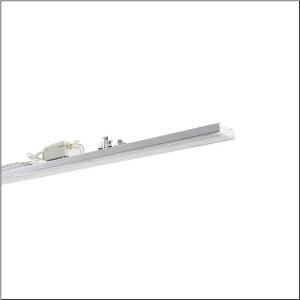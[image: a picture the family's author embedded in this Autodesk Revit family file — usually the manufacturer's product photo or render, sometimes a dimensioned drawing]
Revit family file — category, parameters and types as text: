
# Revit family: licross_21_recessed_mo_52tl1edn465g
name_source: partatom
category: Lighting Fixtures
units: mm (PartAtom-declared; Revit-internal decimal feet)

## family parameters
Cut with Voids When Loaded = No
Host = Face
Light Source = No
Part Type = Normal
Room Calculation Point = No
Round Connector Dimension = Use Diameter
Shared = No

## types (1)
- --- (1 x LED, 6990 lm, 39.3 W, 4000K)
    Apparent Load = 39 VA
    CIE Flux Codes = 85 95 99 100 100
    Color Rendering = 80
    Color Temperature = 4000K
    Default Elevation = 1800 mm
    Description = Licross 21 Recessed MO, luminaire insert, of sheet steel, galvanised, coil coated, white, length: 1.500mm, width: 66mm, height: 67mm, LED rated luminous flux: 6.990lm, light colour: 840, SDCM (Standard Deviation of Colour Matching)MacAdam ≤ 3 SDCM (initial), control gear: DALI 2, with plug, 5-pole, with phase selection, mains connection: 220..240V, AC, 50/60Hz, rated input power: 39W, internal wiring halogen-free, primary light control with lens, of plastic, primary optical cover: cover, of PMMA, light emission: direct distribution, primary light characteristic: symmetric, protection rating (complete): IP40, insulation class (complete): insulation class I (protective earthing), certification: CE, ENEC, VDE, UKCA, protection symbol: D if used in an environment without relevant dust loads with corresponding accessories, impact resistance: IK06, permissible ambient temperature for indoor applications: -25..+40°C, corresponds to IFS (International Featured Standards) requirements for safety and quality in the food industry, reducing of maximum allowable ambient temperature of 5°C with ceiling mounting, LABS conformity tested according to VDMA 24364:2018-05, The light source and the operating device comply with the requirements of the Ecodesign Regulation (EU) 2019/2020 and are replaceable in accordance with this regulation, packaging unit: 1 piece
    Height = 58 mm
    Lamp = 1 x LED
    Lamp Light Flux = 6990 lm
    Lamp Power = 39.3 W
    Lamp count = 1
    Length = 1500 mm
    Luminous efficacy = 178 lm/W
    Manufacturer = Siteco
    ModVariant = No
    Model = 52TL1EDN465G
    Mounting Place = Ceiling
    Mounting Type = Pendant
    Number of Poles = 1
    OnlyDefault = Yes
    Power Factor = 1
    Product Name = Licross 21 Recessed MO
    Product group = luminaire insert | ceiling pendant
    ProductGroupID = 901
    Protection Class = Protection class I
    Protection Degree = IP 40
    RLX_Detail_Level = 1
    RLX_Emergency_Light_Flux = 0 lm
    RLX_Emergency_Type = 0
    RLX_Emergency_Type_DB = No
    RlxData = <blob elided: 24573 chars, md5=8e66deb6>
    Socket = socket
    Standby Power = 0 W
    System Light Flux = 6990 lm
    System Power = 39 W
    Type Comments = factory setting: luminous flux: 100 % | dim-lin: 254 | 267 mA
    Type Image = l_1296930.jpg
    URL = http://relux.com
    VarID = @adj_127065
    Voltage = 0 V
    Weight = 0.00 kg
    Width = 66 mm

## geometry (parser evidence)
native form markers: Blend x4, Sweep x10
no freeform markers — native parametric forms only
